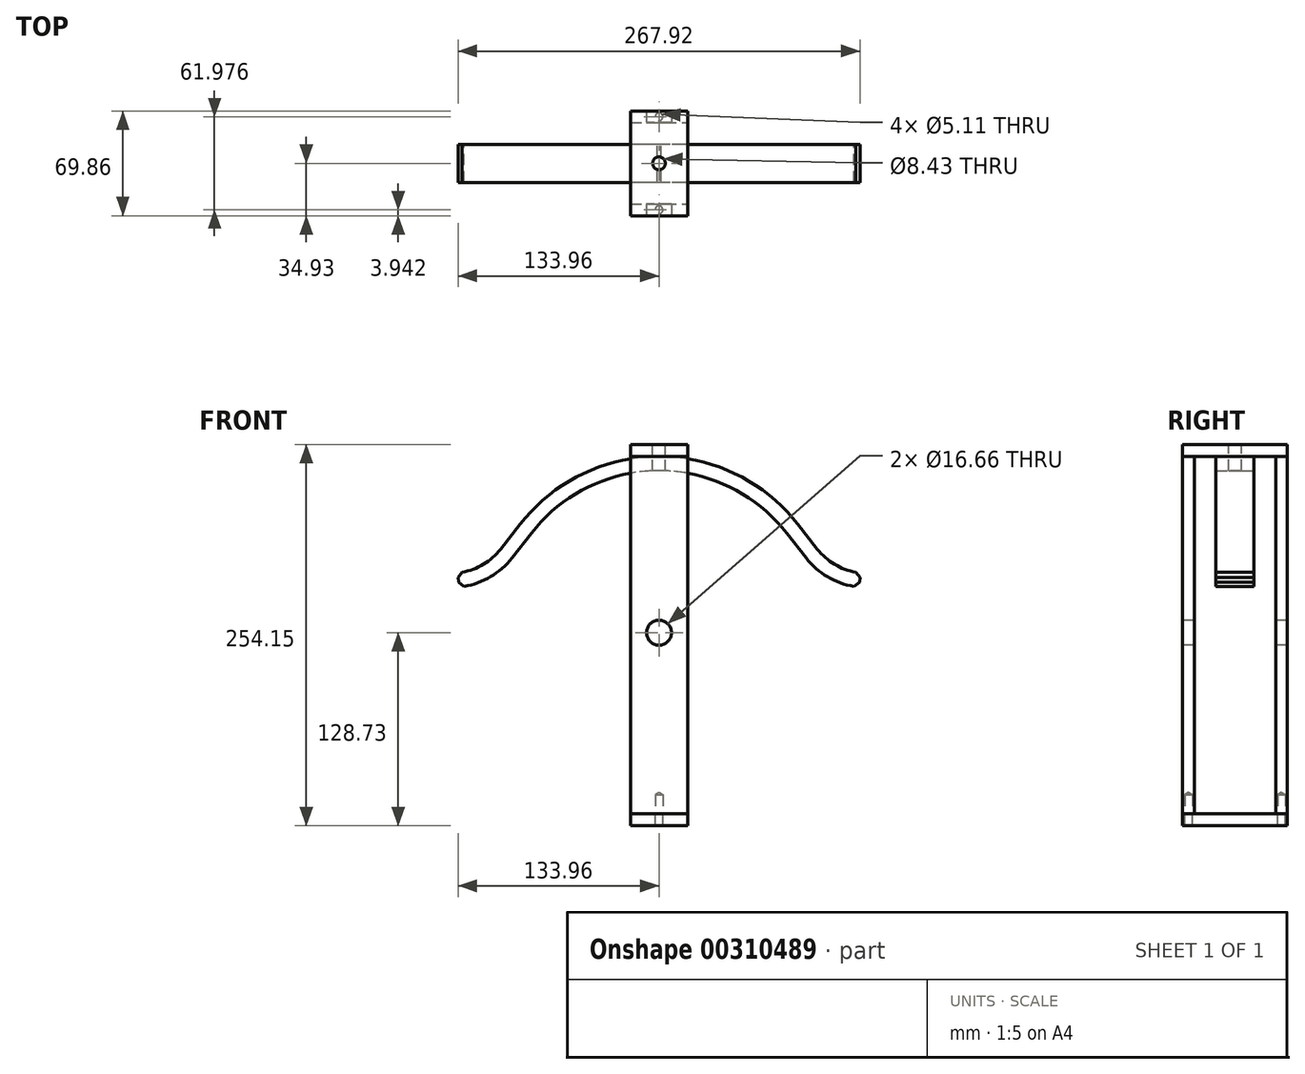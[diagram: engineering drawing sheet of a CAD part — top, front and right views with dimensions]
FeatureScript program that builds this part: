
annotation { "Feature Type Name" : "Feature", "Feature Type Description" : "" }
export const myFeature = defineFeature(function(context is Context, id is Id, definition is map)
    precondition{}
    {
        {
            var Q0;
            Q0=qCreatedBy(makeId("Front.planeOp"),FACE);
            var sketch = newSketch(context, id + "F0", { "sketchPlane" : qUnion([Q0])});
            skArc(sketch, "E0", {"start": v(-104.1, 28.57) * mm, "mid": v(0, -107.95) * mm, "end": v(104.1, 28.57) * mm});
            skArc(sketch, "E1.0", {"start": v(-113.95, 28.57) * mm, "mid": v(0, -117.48) * mm, "end": v(113.95, 28.58) * mm});
            skLineSegment(sketch, "E2", {"start": v(0, 140.03) * mm, "end": v(0, -149.62) * mm, "construction": true});
            skLineSegment(sketch, "E3", {"start": v(-208.33, 0) * mm, "end": v(172.38, 0) * mm, "construction": true});
            skLineSegment(sketch, "E4.0", {"start": v(-138.18, 140.03) * mm, "end": v(-138.18, -149.62) * mm, "construction": true});
            skLineSegment(sketch, "E5.0", {"start": v(-208.33, 28.58) * mm, "end": v(172.38, 28.58) * mm, "construction": true});
            skLineSegment(sketch, "E6.0", {"start": v(-208.33, 80.98) * mm, "end": v(172.38, 80.98) * mm, "construction": true});
            skArc(sketch, "E7", {"start": v(-133.35, 30.4) * mm, "mid": v(-113.75, 36.43) * mm, "end": v(-98.13, 49.72) * mm});
            skLineSegment(sketch, "E8", {"start": v(-85.1, 66.41) * mm, "end": v(-98.13, 49.72) * mm});
            skLineSegment(sketch, "E9.0", {"start": v(-133.35, 140.03) * mm, "end": v(-133.35, -149.62) * mm, "construction": true});
            skArc(sketch, "E10.trimOffspring", {"start": v(-87.44, 78.45) * mm, "mid": v(-87.4, 79.71) * mm, "end": v(-87.38, 80.98) * mm});
            skArc(sketch, "E11.0", {"start": v(-134.25, 39.89) * mm, "mid": v(-118.33, 44.79) * mm, "end": v(-105.64, 55.58) * mm});
            skLineSegment(sketch, "E11.1", {"start": v(-92.61, 72.27) * mm, "end": v(-105.64, 55.58) * mm});
            skLineSegment(sketch, "E12", {"start": v(-133.35, 30.4) * mm, "end": v(-134.25, 39.89) * mm});
            skLineSegment(sketch, "E13.MirrorCS", {"start": v(133.35, 30.4) * mm, "end": v(134.25, 39.89) * mm});
            skArc(sketch, "E14.MirrorCS", {"start": v(87.44, 78.45) * mm, "mid": v(87.4, 79.71) * mm, "end": v(87.38, 80.98) * mm});
            skLineSegment(sketch, "E15.MirrorCS", {"start": v(85.1, 66.41) * mm, "end": v(98.13, 49.72) * mm});
            skLineSegment(sketch, "E16.MirrorCS", {"start": v(92.61, 72.27) * mm, "end": v(105.64, 55.58) * mm});
            skArc(sketch, "E17.MirrorCS", {"start": v(134.25, 39.89) * mm, "mid": v(118.33, 44.79) * mm, "end": v(105.64, 55.58) * mm});
            skArc(sketch, "E18.MirrorCS", {"start": v(133.35, 30.4) * mm, "mid": v(113.75, 36.43) * mm, "end": v(98.13, 49.72) * mm});
            skArc(sketch, "E19.trimOffspring", {"start": v(92.61, 72.27) * mm, "mid": v(0, 117.48) * mm, "end": v(-92.61, 72.27) * mm});
            skArc(sketch, "E20.trimOffspring", {"start": v(85.1, 66.41) * mm, "mid": v(0, 107.95) * mm, "end": v(-85.1, 66.41) * mm});
            skSolve(sketch);
        }
        {
            var Q0;
            Q0=qSketchRegion(id+"F0",true);
            extrude(context, id + "F1", {"entities" : qUnion([Q0]), "endBound" : BoundingType.SYMMETRIC, "depth" : 25.4 * mm});
        }
        {
            var Q0;
            Q0=makeQuery(id+"F1.opExtrude","SWEPT_EDGE",EDGE,{"disambiguationData":[OSD([sQuery(id+"F0.wireOp",EDGE,"E13.MirrorCS"),sQuery(id+"F0.wireOp",EDGE,"E17.MirrorCS")])]});
            var Q1;
            Q1=makeQuery(id+"F1.opExtrude","SWEPT_EDGE",EDGE,{"disambiguationData":[OSD([sQuery(id+"F0.wireOp",EDGE,"E13.MirrorCS"),sQuery(id+"F0.wireOp",EDGE,"E18.MirrorCS")])]});
            var Q2;
            Q2=makeQuery(id+"F1.opExtrude","SWEPT_EDGE",EDGE,{"disambiguationData":[OSD([sQuery(id+"F0.wireOp",EDGE,"E11.0"),sQuery(id+"F0.wireOp",EDGE,"E12")])]});
            var Q3;
            Q3=makeQuery(id+"F1.opExtrude","SWEPT_EDGE",EDGE,{"disambiguationData":[OSD([sQuery(id+"F0.wireOp",EDGE,"E7"),sQuery(id+"F0.wireOp",EDGE,"E12")])]});
            chamfer(context, id + "F2", {"entities" : qUnion([Q0, Q1, Q2, Q3]), "width" : 3.17 * mm, "tangentPropagation" : true});
        }
        {
            var Q0;
            Q0=qCreatedBy(makeId("Front.planeOp"),FACE);
            var sketch = newSketch(context, id + "F3", { "sketchPlane" : qUnion([Q0])});
            skLineSegment(sketch, "E21", {"start": v(0, -36.18) * mm, "end": v(0, 0) * mm, "construction": true});
            skArc(sketch, "E22.0", {"start": v(92.61, 72.27) * mm, "mid": v(0, 117.48) * mm, "end": v(-92.61, 72.27) * mm, "construction": true});
            skLineSegment(sketch, "E23.trimOffspring", {"start": v(0, 117.47) * mm, "end": v(0, 151.71) * mm, "construction": true});
            skLineSegment(sketch, "E24", {"start": v(0, 117.47) * mm, "end": v(-56.03, 117.47) * mm, "construction": true});
            skLineSegment(sketch, "E25.0", {"start": v(0, 121.44) * mm, "end": v(-56.03, 121.44) * mm, "construction": true});
            skLineSegment(sketch, "E26.bottom", {"start": v(-19.05, 117.47) * mm, "end": v(19.05, 117.47) * mm});
            skLineSegment(sketch, "E26.top", {"start": v(-19.05, 125.42) * mm, "end": v(19.05, 125.42) * mm});
            skLineSegment(sketch, "E26.left", {"start": v(-19.05, 117.47) * mm, "end": v(-19.05, 125.42) * mm});
            skLineSegment(sketch, "E26.right", {"start": v(19.05, 117.47) * mm, "end": v(19.05, 125.42) * mm});
            skPoint(sketch, "E26.middle", {"position": v(0, 121.44) * mm});
            skSolve(sketch);
        }
        {
            var Q0;
            Q0=qSketchRegion(id+"F3",true);
            extrude(context, id + "F4", {"entities" : qUnion([Q0]), "operationType" : NewBodyOperationType.ADD, "endBound" : BoundingType.SYMMETRIC, "depth" : 69.85 * mm});
        }
        {
            var Q0;
            Q0=makeQuery(id+"F4.opExtrude","SWEPT_FACE",FACE,{"disambiguationData":[OSD([sQuery(id+"F3.wireOp",EDGE,"E26.bottom")])]});
            var sketch = newSketch(context, id + "F5", { "sketchPlane" : qUnion([Q0])});
            skLineSegment(sketch, "E27.bottom", {"start": v(-19.05, 34.93) * mm, "end": v(19.05, 34.93) * mm});
            skLineSegment(sketch, "E27.top", {"start": v(-19.05, 27.05) * mm, "end": v(19.05, 27.05) * mm});
            skLineSegment(sketch, "E27.left", {"start": v(-19.05, 34.93) * mm, "end": v(-19.05, 27.05) * mm});
            skLineSegment(sketch, "E27.right", {"start": v(19.05, 34.93) * mm, "end": v(19.05, 27.05) * mm});
            skLineSegment(sketch, "E28", {"start": v(-162.59, 0) * mm, "end": v(157.82, 0) * mm, "construction": true});
            skLineSegment(sketch, "E29.MirrorCS", {"start": v(-19.05, -34.93) * mm, "end": v(-19.05, -27.05) * mm});
            skLineSegment(sketch, "E30.MirrorCS", {"start": v(19.05, -34.93) * mm, "end": v(19.05, -27.05) * mm});
            skLineSegment(sketch, "E31.MirrorCS", {"start": v(-19.05, -34.93) * mm, "end": v(19.05, -34.93) * mm});
            skLineSegment(sketch, "E32.MirrorCS", {"start": v(-19.05, -27.05) * mm, "end": v(19.05, -27.05) * mm});
            skSolve(sketch);
        }
        {
            var Q0;
            Q0=qSketchRegion(id+"F5",true);
            extrude(context, id + "F6", {"entities" : qUnion([Q0]), "depth" : 238.25 * mm});
        }
        {
            var Q0;
            Q0=makeQuery(id+"F6.boolean.opBoolean","MERGE",FACE,{"derivedFrom":[makeQuery(id+"F4.opExtrude","CAP_FACE",FACE,{"disambiguationData":[OSD([sQuery(id+"F3.wireOp",EDGE,"E26.bottom"),sQuery(id+"F3.wireOp",EDGE,"E26.top"),sQuery(id+"F3.wireOp",EDGE,"E26.left"),sQuery(id+"F3.wireOp",EDGE,"E26.right")])],"isStart":false}),makeQuery(id+"F6.opExtrude","SWEPT_FACE",FACE,{"disambiguationData":[OSD([sQuery(id+"F5.wireOp",EDGE,"E27.bottom")])]})]});
            var sketch = newSketch(context, id + "F7", { "sketchPlane" : qUnion([Q0])});
            skLineSegment(sketch, "E33.0", {"start": v(-19.05, 125.42) * mm, "end": v(19.05, 125.42) * mm, "construction": true});
            skLineSegment(sketch, "E34", {"start": v(0, 125.42) * mm, "end": v(0, -0.06) * mm, "construction": true});
            skPoint(sketch, "E34.endSnap0", {"position": v(0, 125.42) * mm});
            skPoint(sketch, "E35", {"position": v(0, 0) * mm});
            skSolve(sketch);
        }
        {
            var Q0;
            Q0=sQuery(id+"F7.wireOp",VERTEX,"E35");
            var Q1;
            Q1=makeQuery(id+"F6.opExtrude","SWEPT_BODY",BODY,{"disambiguationData":[OSD([sQuery(id+"F5.wireOp",EDGE,"E29.MirrorCS"),sQuery(id+"F5.wireOp",EDGE,"E30.MirrorCS"),sQuery(id+"F5.wireOp",EDGE,"E31.MirrorCS"),sQuery(id+"F5.wireOp",EDGE,"E32.MirrorCS")])]});
            var Q2;
            Q2=makeQuery(id+"F6.opExtrude","SWEPT_BODY",BODY,{"disambiguationData":[OSD([sQuery(id+"F5.wireOp",EDGE,"E27.bottom"),sQuery(id+"F5.wireOp",EDGE,"E27.top"),sQuery(id+"F5.wireOp",EDGE,"E27.left"),sQuery(id+"F5.wireOp",EDGE,"E27.right")])]});
            hole(context, id + "F8", {"style" : HoleStyle.SIMPLE, "endStyle" : HoleEndStyle.THROUGH, "holeDiameter" : 16.66 * mm, "tappedDepth" : 24.13 * mm, "tapClearance" : 3, "startFromSketch" : true, "locations" : qUnion([Q0]), "scope" : qUnion([Q1, Q2])});
        }
        {
            var Q0;
            Q0=makeQuery(id+"F6.opExtrude","CAP_FACE",FACE,{"disambiguationData":[OSD([sQuery(id+"F5.wireOp",EDGE,"E27.bottom"),sQuery(id+"F5.wireOp",EDGE,"E27.top"),sQuery(id+"F5.wireOp",EDGE,"E27.left"),sQuery(id+"F5.wireOp",EDGE,"E27.right")])],"isStart":false});
            var sketch = newSketch(context, id + "F9", { "sketchPlane" : qUnion([Q0])});
            skLineSegment(sketch, "E36", {"start": v(0, 34.93) * mm, "end": v(0, -34.89) * mm, "construction": true});
            skLineSegment(sketch, "E37", {"start": v(-19.05, 30.99) * mm, "end": v(6.98, 30.99) * mm, "construction": true});
            skLineSegment(sketch, "E38.0", {"start": v(19.05, -27.05) * mm, "end": v(19.05, -34.93) * mm, "construction": true});
            skLineSegment(sketch, "E39", {"start": v(19.05, -30.99) * mm, "end": v(-5.8, -30.99) * mm, "construction": true});
            skPoint(sketch, "E40", {"position": v(0, 30.99) * mm});
            skPoint(sketch, "E41", {"position": v(0, -30.99) * mm});
            skSolve(sketch);
        }
        {
            var Q0;
            Q0=sQuery(id+"F9.wireOp",VERTEX,"E40");
            var Q1;
            Q1=sQuery(id+"F9.wireOp",VERTEX,"E41");
            var Q2;
            Q2=makeQuery(id+"F1.opExtrude","SWEPT_BODY",BODY,{"disambiguationData":[OSD([sQuery(id+"F0.wireOp",EDGE,"E7"),sQuery(id+"F0.wireOp",EDGE,"E8"),sQuery(id+"F0.wireOp",EDGE,"E11.0"),sQuery(id+"F0.wireOp",EDGE,"E11.1"),sQuery(id+"F0.wireOp",EDGE,"E12"),sQuery(id+"F0.wireOp",EDGE,"E13.MirrorCS"),sQuery(id+"F0.wireOp",EDGE,"E15.MirrorCS"),sQuery(id+"F0.wireOp",EDGE,"E16.MirrorCS"),sQuery(id+"F0.wireOp",EDGE,"E17.MirrorCS"),sQuery(id+"F0.wireOp",EDGE,"E18.MirrorCS"),sQuery(id+"F0.wireOp",EDGE,"E19.trimOffspring"),sQuery(id+"F0.wireOp",EDGE,"E20.trimOffspring")])]});
            var Q3;
            Q3=makeQuery(id+"F6.opExtrude","SWEPT_BODY",BODY,{"disambiguationData":[OSD([sQuery(id+"F5.wireOp",EDGE,"E27.bottom"),sQuery(id+"F5.wireOp",EDGE,"E27.top"),sQuery(id+"F5.wireOp",EDGE,"E27.left"),sQuery(id+"F5.wireOp",EDGE,"E27.right")])]});
            var Q4;
            Q4=makeQuery(id+"F6.opExtrude","SWEPT_BODY",BODY,{"disambiguationData":[OSD([sQuery(id+"F5.wireOp",EDGE,"E29.MirrorCS"),sQuery(id+"F5.wireOp",EDGE,"E30.MirrorCS"),sQuery(id+"F5.wireOp",EDGE,"E31.MirrorCS"),sQuery(id+"F5.wireOp",EDGE,"E32.MirrorCS")])]});
            hole(context, id + "F10", {"style" : HoleStyle.SIMPLE, "endStyle" : HoleEndStyle.BLIND, "standardTappedOrClearance" : lookupTablePath({ "standard" : "ANSI", "fit" : "Normal (ASME)", "size" : "#10", "type" : "Clearance" }), "standardBlindInLast" : lookupTablePath({ "fit" : "Free", "standard" : "ANSI", "size" : "#10", "type" : "Clearance" }), "holeDiameter" : 5.1 * mm, "holeDepth" : 12.7 * mm, "tappedDepth" : 24.13 * mm, "tapClearance" : 3, "startFromSketch" : true, "locations" : qUnion([Q0, Q1]), "scope" : qUnion([Q2, Q3, Q4])});
        }
        {
            var Q0;
            Q0=makeQuery(id+"F4.opExtrude","SWEPT_FACE",FACE,{"disambiguationData":[OSD([sQuery(id+"F3.wireOp",EDGE,"E26.top")])]});
            var sketch = newSketch(context, id + "F11", { "sketchPlane" : qUnion([Q0])});
            skLineSegment(sketch, "E42.0.0", {"start": v(19.05, 34.93) * mm, "end": v(-19.05, 34.93) * mm, "construction": true});
            skLineSegment(sketch, "E42.0.1", {"start": v(-19.05, 34.93) * mm, "end": v(-19.05, -34.93) * mm, "construction": true});
            skLineSegment(sketch, "E42.0.2", {"start": v(-19.05, -34.93) * mm, "end": v(19.05, -34.93) * mm, "construction": true});
            skLineSegment(sketch, "E42.0.3", {"start": v(19.05, -34.93) * mm, "end": v(19.05, 34.93) * mm, "construction": true});
            skLineSegment(sketch, "E43", {"start": v(0, 34.93) * mm, "end": v(0, -34.93) * mm, "construction": true});
            skPoint(sketch, "E44", {"position": v(0, 0) * mm});
            skSolve(sketch);
        }
        {
            var Q0;
            Q0=sQuery(id+"F11.wireOp",VERTEX,"E44");
            var Q1;
            Q1=makeQuery(id+"F1.opExtrude","SWEPT_BODY",BODY,{"disambiguationData":[OSD([sQuery(id+"F0.wireOp",EDGE,"E7"),sQuery(id+"F0.wireOp",EDGE,"E8"),sQuery(id+"F0.wireOp",EDGE,"E11.0"),sQuery(id+"F0.wireOp",EDGE,"E11.1"),sQuery(id+"F0.wireOp",EDGE,"E12"),sQuery(id+"F0.wireOp",EDGE,"E13.MirrorCS"),sQuery(id+"F0.wireOp",EDGE,"E15.MirrorCS"),sQuery(id+"F0.wireOp",EDGE,"E16.MirrorCS"),sQuery(id+"F0.wireOp",EDGE,"E17.MirrorCS"),sQuery(id+"F0.wireOp",EDGE,"E18.MirrorCS"),sQuery(id+"F0.wireOp",EDGE,"E19.trimOffspring"),sQuery(id+"F0.wireOp",EDGE,"E20.trimOffspring")])]});
            hole(context, id + "F12", {"style" : HoleStyle.SIMPLE, "endStyle" : HoleEndStyle.BLIND, "standardTappedOrClearance" : lookupTablePath({ "standard" : "ANSI", "engagement" : "75%", "pitch" : "24 tpi", "size" : "3/8", "type" : "Tapped" }), "standardBlindInLast" : lookupTablePath({ "standard" : "ANSI", "engagement" : "75%", "pitch" : "24 tpi", "size" : "3/8", "type" : "Tapped" }), "holeDiameter" : 8.43 * mm, "showTappedDepth" : true, "holeDepth" : 27.3 * mm, "tappedDepth" : 24.13 * mm, "tapClearance" : 3, "startFromSketch" : true, "locations" : qUnion([Q0]), "scope" : qUnion([Q1]), "majorDiameter" : 9.53 * mm});
        }
        {
            var Q0;
            Q0=makeQuery(id+"F6.opExtrude","CAP_FACE",FACE,{"disambiguationData":[OSD([sQuery(id+"F5.wireOp",EDGE,"E29.MirrorCS"),sQuery(id+"F5.wireOp",EDGE,"E30.MirrorCS"),sQuery(id+"F5.wireOp",EDGE,"E31.MirrorCS"),sQuery(id+"F5.wireOp",EDGE,"E32.MirrorCS")])],"isStart":false});
            var sketch = newSketch(context, id + "F13", { "sketchPlane" : qUnion([Q0])});
            skLineSegment(sketch, "E45.0", {"start": v(-19.05, 34.93) * mm, "end": v(19.05, 34.93) * mm, "construction": true});
            skLineSegment(sketch, "E46.0", {"start": v(-19.05, -34.93) * mm, "end": v(19.05, -34.93) * mm, "construction": true});
            skLineSegment(sketch, "E47.bottom", {"start": v(-19.05, -34.93) * mm, "end": v(19.05, -34.93) * mm});
            skLineSegment(sketch, "E47.top", {"start": v(-19.05, 34.93) * mm, "end": v(19.05, 34.93) * mm});
            skLineSegment(sketch, "E47.left", {"start": v(-19.05, -34.93) * mm, "end": v(-19.05, 34.93) * mm});
            skLineSegment(sketch, "E47.right", {"start": v(19.05, -34.93) * mm, "end": v(19.05, 34.93) * mm});
            skCircle(sketch, "E48.0", {"center": v(0, -30.99) * mm, "radius": 2.55 * mm});
            skCircle(sketch, "E49.0", {"center": v(0, 30.99) * mm, "radius": 2.55 * mm});
            skSolve(sketch);
        }
        {
            var Q0;
            Q0=qSketchRegion(id+"F13",true);
            extrude(context, id + "F14", {"entities" : qUnion([Q0]), "depth" : 7.95 * mm});
        }
    });
